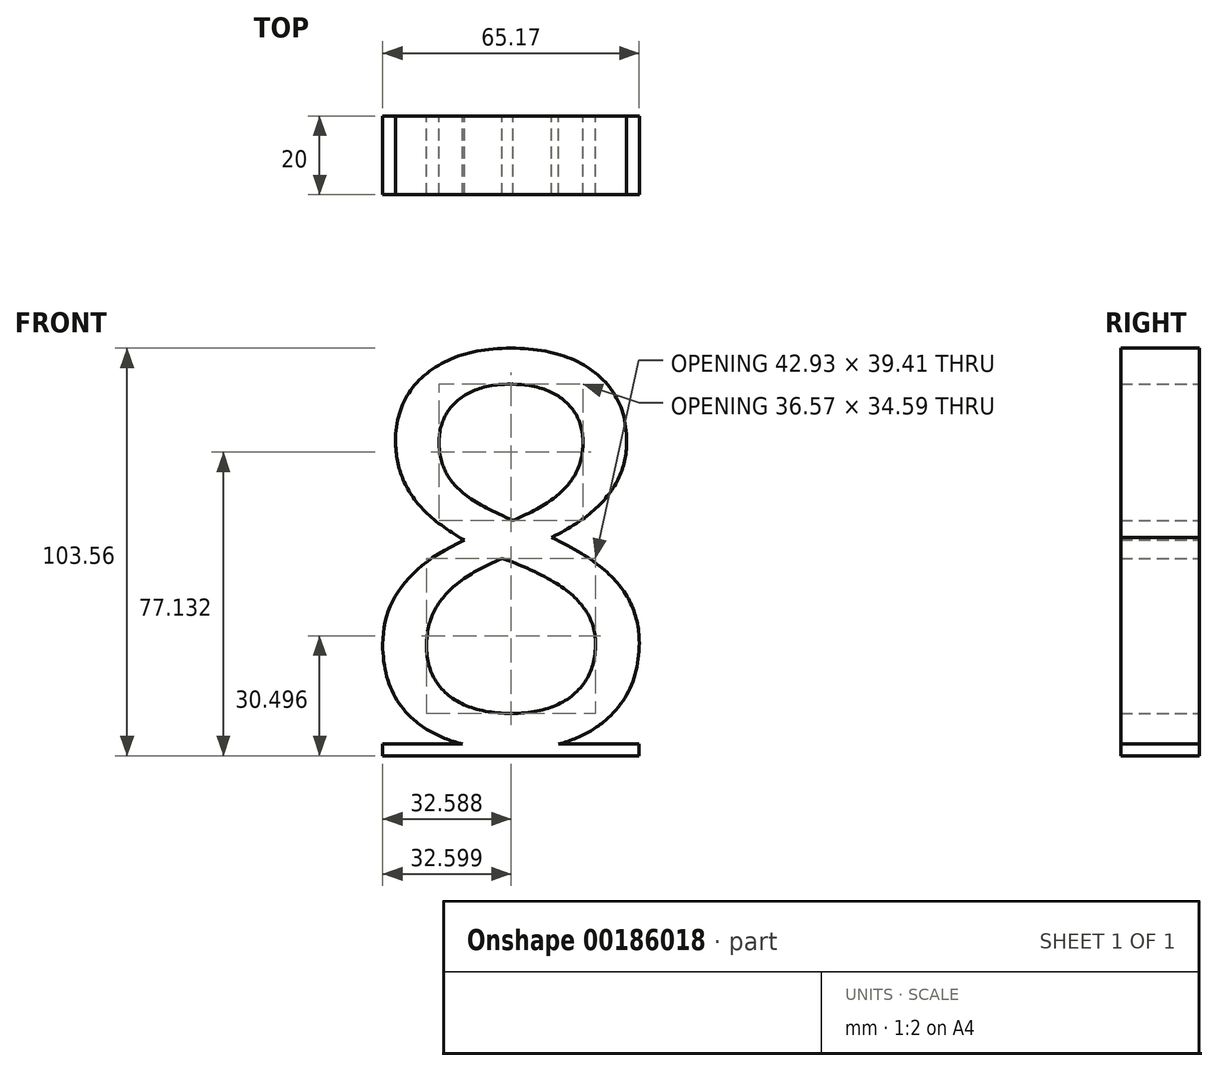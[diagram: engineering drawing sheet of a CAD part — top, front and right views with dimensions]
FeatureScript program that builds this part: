
annotation { "Feature Type Name" : "Feature", "Feature Type Description" : "" }
export const myFeature = defineFeature(function(context is Context, id is Id, definition is map)
    precondition{}
    {
        {
            var Q0;
            Q0=qCreatedBy(makeId("Front.planeOp"),FACE);
            var sketch = newSketch(context, id + "F0", { "sketchPlane" : qUnion([Q0])});
            skText(sketch, "E0", { "text": "8\n", "fontName": "OpenSans-Regular.ttf"});
            const initialGuessF0  = {"E0": [-0.04061, 0, 1, 0, 0.1]};
            skSetInitialGuess(sketch, initialGuessF0);
            skSolve(sketch);
        }
        {
            var Q0;
            Q0=makeQuery(id+"F0.imprint","IMPRINT",FACE,{"disambiguationData":[TD([[makeQuery(id+"F0.imprint","IMPRINT",EDGE,{"derivedFrom":sQuery(id+"F0.wireOp",EDGE,"E0.sketch_text.stroke-0")}),-1.0]])]});
            extrude(context, id + "F1", {"entities" : qUnion([Q0]), "depth" : 10 * mm, "hasSecondDirection" : true, "secondDirectionOppositeDirection" : true, "secondDirectionDepth" : 10 * mm});
        }
        {
            var Q0;
            Q0=qCreatedBy(makeId("Top.planeOp"),FACE);
            var sketch = newSketch(context, id + "F2", { "sketchPlane" : qUnion([Q0])});
            skLineSegment(sketch, "E1.bottom", {"start": v(31.6, 10) * mm, "end": v(-33.56, 10) * mm});
            skLineSegment(sketch, "E1.top", {"start": v(31.6, -10) * mm, "end": v(-33.56, -10) * mm});
            skLineSegment(sketch, "E1.left", {"start": v(-33.56, 10) * mm, "end": v(-33.56, -10) * mm});
            skLineSegment(sketch, "E1.right", {"start": v(31.6, 10) * mm, "end": v(31.6, -10) * mm});
            skSolve(sketch);
        }
        {
            var Q0;
            Q0=qSketchRegion(id+"F2",true);
            extrude(context, id + "F3", {"entities" : qUnion([Q0]), "operationType" : NewBodyOperationType.ADD, "oppositeDirection" : true, "depth" : 3 * mm});
        }
    });
